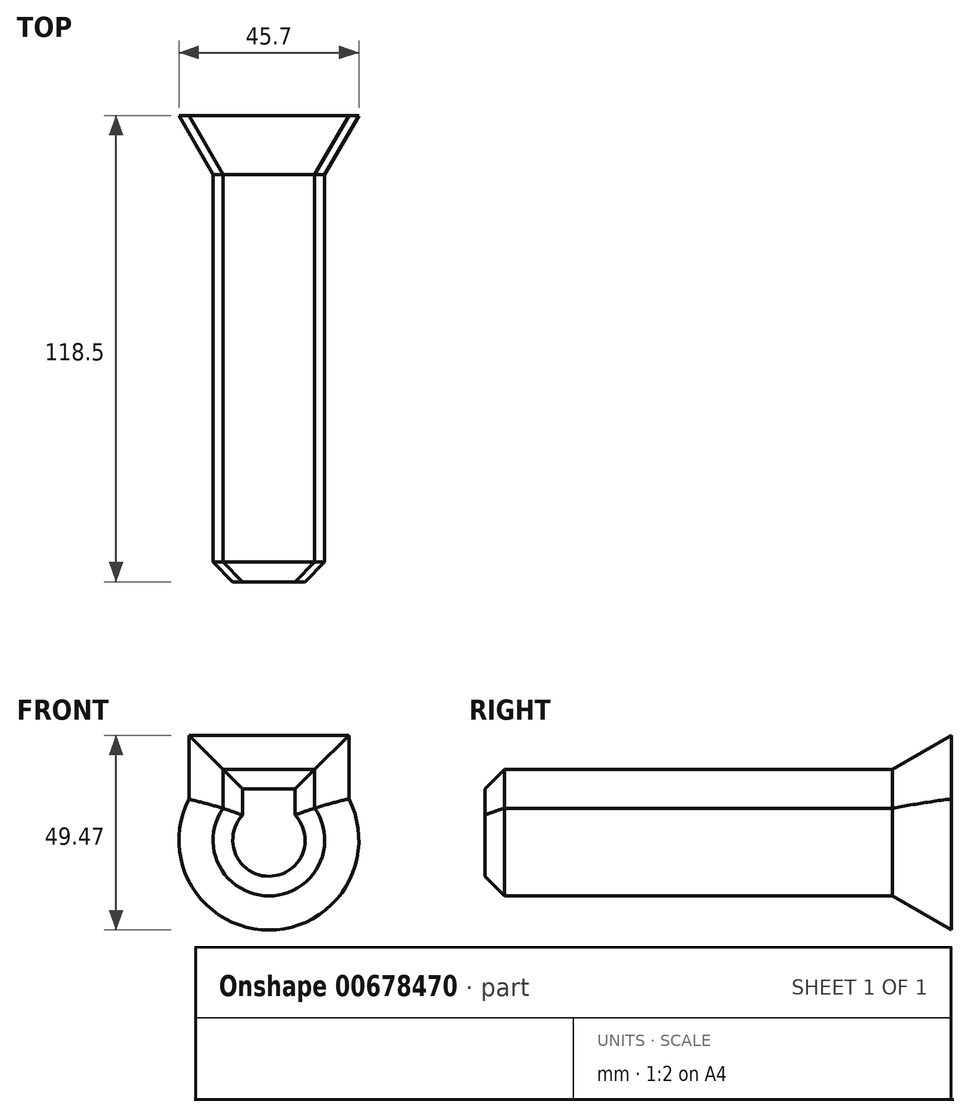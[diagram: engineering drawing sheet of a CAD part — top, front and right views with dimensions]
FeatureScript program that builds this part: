
annotation { "Feature Type Name" : "Feature", "Feature Type Description" : "" }
export const myFeature = defineFeature(function(context is Context, id is Id, definition is map)
    precondition{}
    {
        {
            var Q0;
            Q0=qCreatedBy(makeId("Front.planeOp"),FACE);
            var sketch = newSketch(context, id + "F0", { "sketchPlane" : qUnion([Q0])});
            skCircle(sketch, "E0", {"center": v(0, 0) * mm, "radius": 14.2 * mm});
            skLineSegment(sketch, "E1", {"start": v(-11.68, 8.07) * mm, "end": v(-11.68, 17.96) * mm});
            skLineSegment(sketch, "E2", {"start": v(-11.68, 17.96) * mm, "end": v(11.64, 17.96) * mm});
            skLineSegment(sketch, "E3", {"start": v(11.64, 17.96) * mm, "end": v(11.64, 8.12) * mm});
            skSolve(sketch);
        }
        {
            var Q0;
            {var subQ0=sQuery(id+"F0.wireOp",EDGE,"E0");var subQ1=makeQuery(id+"F0.imprint","INTERSECT",VERTEX,{"derivedFrom":[subQ0,sQuery(id+"F0.wireOp",EDGE,"E1")]});Q0=makeQuery(id+"F0.imprint","IMPRINT",FACE,{"disambiguationData":[TD([[makeQuery(id+"F0.imprint","IMPRINT",EDGE,{"disambiguationData":[TD([[subQ1,1.0]])],"derivedFrom":subQ0}),1.0]])]});}
            var Q1;
            {var subQ0=sQuery(id+"F0.wireOp",EDGE,"E1");Q1=makeQuery(id+"F0.imprint","IMPRINT",FACE,{"disambiguationData":[TD([[makeQuery(id+"F0.imprint","IMPRINT",EDGE,{"derivedFrom":subQ0}),-1.0]])]});}
            extrude(context, id + "F1", {"entities" : qUnion([Q0, Q1]), "depth" : 103.5 * mm, "offsetDistance" : 25 * mm});
        }
        {
            var Q0;
            Q0=makeQuery(id+"F1.opExtrude","CAP_FACE",FACE,{"disambiguationData":[OSD([sQuery(id+"F0.wireOp",EDGE,"E0"),sQuery(id+"F0.wireOp",EDGE,"E1"),sQuery(id+"F0.wireOp",EDGE,"E2"),sQuery(id+"F0.wireOp",EDGE,"E3")])],"isStart":true});
            extrude(context, id + "F2", {"entities" : qUnion([Q0]), "operationType" : NewBodyOperationType.ADD, "depth" : 15 * mm, "offsetDistance" : 25 * mm, "hasDraft" : true, "draftAngle" : 30 * degree});
        }
        {
            var Q0;
            Q0=makeQuery(id+"F1.opExtrude","CAP_FACE",FACE,{"disambiguationData":[OSD([sQuery(id+"F0.wireOp",EDGE,"E0"),sQuery(id+"F0.wireOp",EDGE,"E1"),sQuery(id+"F0.wireOp",EDGE,"E2"),sQuery(id+"F0.wireOp",EDGE,"E3")])],"isStart":false});
            chamfer(context, id + "F3", {"entities" : qUnion([Q0]), "width" : 5 * mm, "tangentPropagation" : true});
        }
    });
